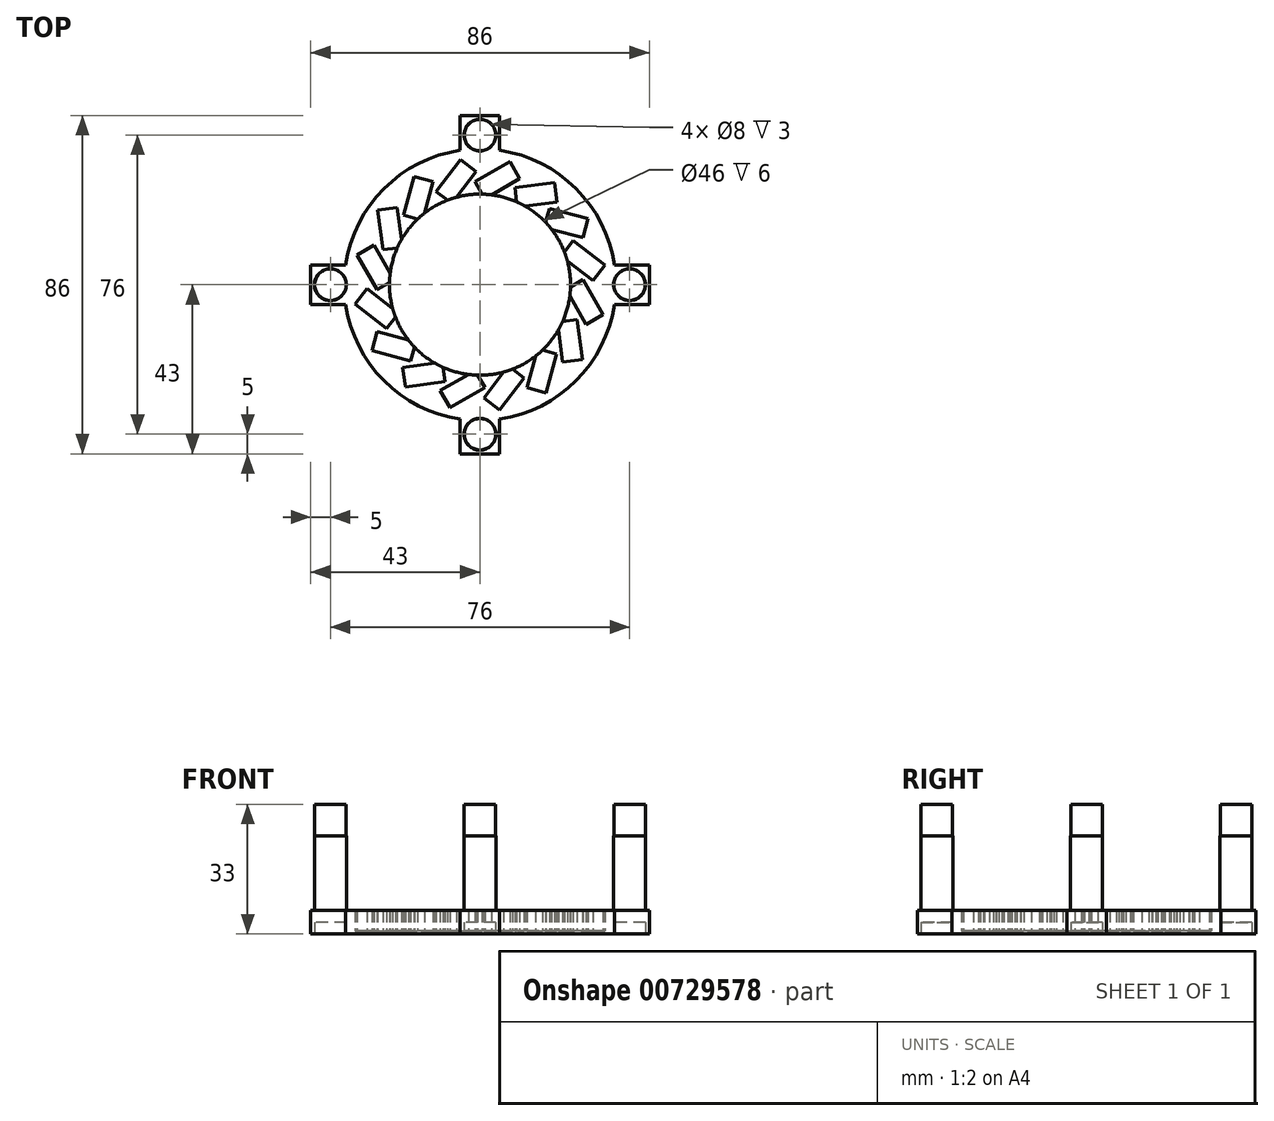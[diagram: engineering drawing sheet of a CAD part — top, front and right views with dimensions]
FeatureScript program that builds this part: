
annotation { "Feature Type Name" : "Feature", "Feature Type Description" : "" }
export const myFeature = defineFeature(function(context is Context, id is Id, definition is map)
    precondition{}
    {
        {
            var Q0;
            Q0=qCreatedBy(makeId("Top.planeOp"),FACE);
            var sketch = newSketch(context, id + "F0", { "sketchPlane" : qUnion([Q0])});
            skCircle(sketch, "E0", {"center": v(0, 0) * mm, "radius": 23 * mm});
            skCircle(sketch, "E1", {"center": v(0, 0) * mm, "radius": 34 * mm});
            skLineSegment(sketch, "E2", {"start": v(0, 0) * mm, "end": v(0, 30) * mm, "construction": true});
            skLineSegment(sketch, "E3.bottom", {"start": v(8.43, 31.47) * mm, "end": v(10.03, 29.56) * mm});
            skLineSegment(sketch, "E3.top", {"start": v(0, 24.4) * mm, "end": v(1.6, 22.48) * mm});
            skLineSegment(sketch, "E3.right", {"start": v(10.03, 29.56) * mm, "end": v(1.6, 22.48) * mm});
            skLineSegment(sketch, "E4.MirrorCS", {"start": v(6.82, 33.39) * mm, "end": v(-1.6, 26.32) * mm});
            skLineSegment(sketch, "E5.MirrorCS", {"start": v(0, 24.4) * mm, "end": v(-1.6, 26.32) * mm});
            skLineSegment(sketch, "E6.MirrorCS", {"start": v(8.43, 31.47) * mm, "end": v(6.82, 33.39) * mm});
            skLineSegment(sketch, "E7", {"start": v(0, 0) * mm, "end": v(35, 0) * mm, "construction": true});
            skSolve(sketch);
        }
        {
            var Q0;
            Q0=qCreatedBy(makeId("Top.planeOp"),FACE);
            var sketch = newSketch(context, id + "F1", { "sketchPlane" : qUnion([Q0])});
            skCircle(sketch, "E8", {"center": v(0, 0) * mm, "radius": 23 * mm});
            skArc(sketch, "E9", {"start": v(-34.4, -2.7) * mm, "mid": v(-24.4, -24.4) * mm, "end": v(-2.7, -34.4) * mm});
            skArc(sketch, "E10", {"start": v(-33.94, -1.95) * mm, "mid": v(-24.04, -24.04) * mm, "end": v(-1.95, -33.94) * mm});
            skLineSegment(sketch, "E11", {"start": v(0, 0) * mm, "end": v(0, 12.6) * mm, "construction": true});
            skLineSegment(sketch, "E12.bottom", {"start": v(8.83, 29.1) * mm, "end": v(10.08, 26.93) * mm});
            skLineSegment(sketch, "E12.top", {"start": v(0, 24) * mm, "end": v(1.25, 21.83) * mm});
            skLineSegment(sketch, "E12.right", {"start": v(10.08, 26.93) * mm, "end": v(1.25, 21.83) * mm});
            skLineSegment(sketch, "E13.MirrorCS", {"start": v(7.58, 31.27) * mm, "end": v(-1.25, 26.17) * mm});
            skLineSegment(sketch, "E14.MirrorCS", {"start": v(0, 24) * mm, "end": v(-1.25, 26.17) * mm});
            skLineSegment(sketch, "E15.MirrorCS", {"start": v(8.83, 29.1) * mm, "end": v(7.58, 31.27) * mm});
            skLineSegment(sketch, "E16", {"start": v(0, 0) * mm, "end": v(34, 0) * mm, "construction": true});
            skLineSegment(sketch, "E17.1.0", {"start": v(-4.96, 31.79) * mm, "end": v(-11.17, 23.7) * mm});
            skLineSegment(sketch, "E17.1.1", {"start": v(-2.98, 30.27) * mm, "end": v(-4.96, 31.79) * mm});
            skLineSegment(sketch, "E17.1.2", {"start": v(-2.98, 30.27) * mm, "end": v(-1, 28.74) * mm});
            skLineSegment(sketch, "E17.1.3", {"start": v(-1, 28.74) * mm, "end": v(-7.2, 20.65) * mm});
            skLineSegment(sketch, "E17.1.4", {"start": v(-9.18, 22.17) * mm, "end": v(-7.2, 20.65) * mm});
            skLineSegment(sketch, "E17.1.5", {"start": v(-9.18, 22.17) * mm, "end": v(-11.17, 23.7) * mm});
            skLineSegment(sketch, "E17.2.0", {"start": v(-16.75, 27.47) * mm, "end": v(-19.39, 17.62) * mm});
            skLineSegment(sketch, "E17.2.1", {"start": v(-14.33, 26.82) * mm, "end": v(-16.75, 27.47) * mm});
            skLineSegment(sketch, "E17.2.2", {"start": v(-14.33, 26.82) * mm, "end": v(-11.92, 26.18) * mm});
            skLineSegment(sketch, "E17.2.3", {"start": v(-11.92, 26.18) * mm, "end": v(-14.56, 16.32) * mm});
            skLineSegment(sketch, "E17.2.4", {"start": v(-16.97, 16.97) * mm, "end": v(-14.56, 16.32) * mm});
            skLineSegment(sketch, "E17.2.5", {"start": v(-16.97, 16.97) * mm, "end": v(-19.39, 17.62) * mm});
            skLineSegment(sketch, "E17.3.0", {"start": v(-25.98, 18.97) * mm, "end": v(-24.65, 8.86) * mm});
            skLineSegment(sketch, "E17.3.1", {"start": v(-23.5, 19.3) * mm, "end": v(-25.98, 18.97) * mm});
            skLineSegment(sketch, "E17.3.2", {"start": v(-23.5, 19.3) * mm, "end": v(-21.03, 19.62) * mm});
            skLineSegment(sketch, "E17.3.3", {"start": v(-21.03, 19.62) * mm, "end": v(-19.7, 9.51) * mm});
            skLineSegment(sketch, "E17.3.4", {"start": v(-22.17, 9.18) * mm, "end": v(-19.7, 9.51) * mm});
            skLineSegment(sketch, "E17.3.5", {"start": v(-22.17, 9.18) * mm, "end": v(-24.65, 8.86) * mm});
            skLineSegment(sketch, "E17.4.0", {"start": v(-31.27, 7.58) * mm, "end": v(-26.17, -1.25) * mm});
            skLineSegment(sketch, "E17.4.1", {"start": v(-29.1, 8.83) * mm, "end": v(-31.27, 7.58) * mm});
            skLineSegment(sketch, "E17.4.2", {"start": v(-29.1, 8.83) * mm, "end": v(-26.93, 10.08) * mm});
            skLineSegment(sketch, "E17.4.3", {"start": v(-26.93, 10.08) * mm, "end": v(-21.83, 1.25) * mm});
            skLineSegment(sketch, "E17.4.4", {"start": v(-24, 0) * mm, "end": v(-21.83, 1.25) * mm});
            skLineSegment(sketch, "E17.4.5", {"start": v(-24, 0) * mm, "end": v(-26.17, -1.25) * mm});
            skLineSegment(sketch, "E17.5.0", {"start": v(-31.79, -4.96) * mm, "end": v(-23.7, -11.17) * mm});
            skLineSegment(sketch, "E17.5.1", {"start": v(-30.27, -2.98) * mm, "end": v(-31.79, -4.96) * mm});
            skLineSegment(sketch, "E17.5.2", {"start": v(-30.27, -2.98) * mm, "end": v(-28.74, -1) * mm});
            skLineSegment(sketch, "E17.5.3", {"start": v(-28.74, -1) * mm, "end": v(-20.65, -7.2) * mm});
            skLineSegment(sketch, "E17.5.4", {"start": v(-22.17, -9.18) * mm, "end": v(-20.65, -7.2) * mm});
            skLineSegment(sketch, "E17.5.5", {"start": v(-22.17, -9.18) * mm, "end": v(-23.7, -11.17) * mm});
            skLineSegment(sketch, "E17.6.0", {"start": v(-27.47, -16.75) * mm, "end": v(-17.62, -19.39) * mm});
            skLineSegment(sketch, "E17.6.1", {"start": v(-26.82, -14.33) * mm, "end": v(-27.47, -16.75) * mm});
            skLineSegment(sketch, "E17.6.2", {"start": v(-26.82, -14.33) * mm, "end": v(-26.18, -11.92) * mm});
            skLineSegment(sketch, "E17.6.3", {"start": v(-26.18, -11.92) * mm, "end": v(-16.32, -14.56) * mm});
            skLineSegment(sketch, "E17.6.4", {"start": v(-16.97, -16.97) * mm, "end": v(-16.32, -14.56) * mm});
            skLineSegment(sketch, "E17.6.5", {"start": v(-16.97, -16.97) * mm, "end": v(-17.62, -19.39) * mm});
            skLineSegment(sketch, "E17.7.0", {"start": v(-18.97, -25.98) * mm, "end": v(-8.86, -24.65) * mm});
            skLineSegment(sketch, "E17.7.1", {"start": v(-19.3, -23.5) * mm, "end": v(-18.97, -25.98) * mm});
            skLineSegment(sketch, "E17.7.2", {"start": v(-19.3, -23.5) * mm, "end": v(-19.62, -21.03) * mm});
            skLineSegment(sketch, "E17.7.3", {"start": v(-19.62, -21.03) * mm, "end": v(-9.51, -19.7) * mm});
            skLineSegment(sketch, "E17.7.4", {"start": v(-9.18, -22.17) * mm, "end": v(-9.51, -19.7) * mm});
            skLineSegment(sketch, "E17.7.5", {"start": v(-9.18, -22.17) * mm, "end": v(-8.86, -24.65) * mm});
            skLineSegment(sketch, "E17.8.0", {"start": v(-7.58, -31.27) * mm, "end": v(1.25, -26.17) * mm});
            skLineSegment(sketch, "E17.8.1", {"start": v(-8.83, -29.1) * mm, "end": v(-7.58, -31.27) * mm});
            skLineSegment(sketch, "E17.8.2", {"start": v(-8.83, -29.1) * mm, "end": v(-10.08, -26.93) * mm});
            skLineSegment(sketch, "E17.8.3", {"start": v(-10.08, -26.93) * mm, "end": v(-1.25, -21.83) * mm});
            skLineSegment(sketch, "E17.8.4", {"start": v(0, -24) * mm, "end": v(-1.25, -21.83) * mm});
            skLineSegment(sketch, "E17.8.5", {"start": v(0, -24) * mm, "end": v(1.25, -26.17) * mm});
            skLineSegment(sketch, "E17.9.0", {"start": v(4.96, -31.79) * mm, "end": v(11.17, -23.7) * mm});
            skLineSegment(sketch, "E17.9.1", {"start": v(2.98, -30.27) * mm, "end": v(4.96, -31.79) * mm});
            skLineSegment(sketch, "E17.9.2", {"start": v(2.98, -30.27) * mm, "end": v(1, -28.74) * mm});
            skLineSegment(sketch, "E17.9.3", {"start": v(1, -28.74) * mm, "end": v(7.2, -20.65) * mm});
            skLineSegment(sketch, "E17.9.4", {"start": v(9.18, -22.17) * mm, "end": v(7.2, -20.65) * mm});
            skLineSegment(sketch, "E17.9.5", {"start": v(9.18, -22.17) * mm, "end": v(11.17, -23.7) * mm});
            skLineSegment(sketch, "E17.10.0", {"start": v(16.75, -27.47) * mm, "end": v(19.39, -17.62) * mm});
            skLineSegment(sketch, "E17.10.1", {"start": v(14.33, -26.82) * mm, "end": v(16.75, -27.47) * mm});
            skLineSegment(sketch, "E17.10.2", {"start": v(14.33, -26.82) * mm, "end": v(11.92, -26.18) * mm});
            skLineSegment(sketch, "E17.10.3", {"start": v(11.92, -26.18) * mm, "end": v(14.56, -16.32) * mm});
            skLineSegment(sketch, "E17.10.4", {"start": v(16.97, -16.97) * mm, "end": v(14.56, -16.32) * mm});
            skLineSegment(sketch, "E17.10.5", {"start": v(16.97, -16.97) * mm, "end": v(19.39, -17.62) * mm});
            skLineSegment(sketch, "E17.11.0", {"start": v(25.98, -18.97) * mm, "end": v(24.65, -8.86) * mm});
            skLineSegment(sketch, "E17.11.1", {"start": v(23.5, -19.3) * mm, "end": v(25.98, -18.97) * mm});
            skLineSegment(sketch, "E17.11.2", {"start": v(23.5, -19.3) * mm, "end": v(21.03, -19.62) * mm});
            skLineSegment(sketch, "E17.11.3", {"start": v(21.03, -19.62) * mm, "end": v(19.7, -9.51) * mm});
            skLineSegment(sketch, "E17.11.4", {"start": v(22.17, -9.18) * mm, "end": v(19.7, -9.51) * mm});
            skLineSegment(sketch, "E17.11.5", {"start": v(22.17, -9.18) * mm, "end": v(24.65, -8.86) * mm});
            skLineSegment(sketch, "E17.12.0", {"start": v(31.27, -7.58) * mm, "end": v(26.17, 1.25) * mm});
            skLineSegment(sketch, "E17.12.1", {"start": v(29.1, -8.83) * mm, "end": v(31.27, -7.58) * mm});
            skLineSegment(sketch, "E17.12.2", {"start": v(29.1, -8.83) * mm, "end": v(26.93, -10.08) * mm});
            skLineSegment(sketch, "E17.12.3", {"start": v(26.93, -10.08) * mm, "end": v(21.83, -1.25) * mm});
            skLineSegment(sketch, "E17.12.4", {"start": v(24, 0) * mm, "end": v(21.83, -1.25) * mm});
            skLineSegment(sketch, "E17.12.5", {"start": v(24, 0) * mm, "end": v(26.17, 1.25) * mm});
            skLineSegment(sketch, "E17.13.0", {"start": v(31.79, 4.96) * mm, "end": v(23.7, 11.17) * mm});
            skLineSegment(sketch, "E17.13.1", {"start": v(30.27, 2.98) * mm, "end": v(31.79, 4.96) * mm});
            skLineSegment(sketch, "E17.13.2", {"start": v(30.27, 2.98) * mm, "end": v(28.74, 1) * mm});
            skLineSegment(sketch, "E17.13.3", {"start": v(28.74, 1) * mm, "end": v(20.65, 7.2) * mm});
            skLineSegment(sketch, "E17.13.4", {"start": v(22.17, 9.18) * mm, "end": v(20.65, 7.2) * mm});
            skLineSegment(sketch, "E17.13.5", {"start": v(22.17, 9.18) * mm, "end": v(23.7, 11.17) * mm});
            skLineSegment(sketch, "E17.14.0", {"start": v(27.47, 16.75) * mm, "end": v(17.62, 19.39) * mm});
            skLineSegment(sketch, "E17.14.1", {"start": v(26.82, 14.33) * mm, "end": v(27.47, 16.75) * mm});
            skLineSegment(sketch, "E17.14.2", {"start": v(26.82, 14.33) * mm, "end": v(26.18, 11.92) * mm});
            skLineSegment(sketch, "E17.14.3", {"start": v(26.18, 11.92) * mm, "end": v(16.32, 14.56) * mm});
            skLineSegment(sketch, "E17.14.4", {"start": v(16.97, 16.97) * mm, "end": v(16.32, 14.56) * mm});
            skLineSegment(sketch, "E17.14.5", {"start": v(16.97, 16.97) * mm, "end": v(17.62, 19.39) * mm});
            skLineSegment(sketch, "E17.15.0", {"start": v(18.97, 25.98) * mm, "end": v(8.86, 24.65) * mm});
            skLineSegment(sketch, "E17.15.1", {"start": v(19.3, 23.5) * mm, "end": v(18.97, 25.98) * mm});
            skLineSegment(sketch, "E17.15.2", {"start": v(19.3, 23.5) * mm, "end": v(19.62, 21.03) * mm});
            skLineSegment(sketch, "E17.15.3", {"start": v(19.62, 21.03) * mm, "end": v(9.51, 19.7) * mm});
            skLineSegment(sketch, "E17.15.4", {"start": v(9.18, 22.17) * mm, "end": v(9.51, 19.7) * mm});
            skLineSegment(sketch, "E17.15.5", {"start": v(9.18, 22.17) * mm, "end": v(8.86, 24.65) * mm});
            skCircle(sketch, "E18", {"center": v(0, 38) * mm, "radius": 4 * mm});
            skCircle(sketch, "E19", {"center": v(0, 38) * mm, "radius": 4.5 * mm});
            skLineSegment(sketch, "E20", {"start": v(0, 42.5) * mm, "end": v(0, 43) * mm});
            skLineSegment(sketch, "E21", {"start": v(0, 43) * mm, "end": v(5, 43) * mm});
            skLineSegment(sketch, "E22", {"start": v(5, 43) * mm, "end": v(5, 34.14) * mm});
            skLineSegment(sketch, "E23.MirrorCS", {"start": v(0, 43) * mm, "end": v(-5, 43) * mm});
            skLineSegment(sketch, "E24.MirrorCS", {"start": v(-5, 43) * mm, "end": v(-5, 34.14) * mm});
            skLineSegment(sketch, "E25.1.0", {"start": v(-43, 0) * mm, "end": v(-43, 5) * mm});
            skLineSegment(sketch, "E25.1.1", {"start": v(-43, 5) * mm, "end": v(-34.14, 5) * mm});
            skLineSegment(sketch, "E25.1.2", {"start": v(-43, 0) * mm, "end": v(-43, -5) * mm});
            skLineSegment(sketch, "E25.1.3", {"start": v(-43, -5) * mm, "end": v(-34.14, -5) * mm});
            skCircle(sketch, "E25.1.4", {"center": v(-38, 0) * mm, "radius": 4.5 * mm});
            skCircle(sketch, "E25.1.5", {"center": v(-38, 0) * mm, "radius": 4 * mm});
            skLineSegment(sketch, "E25.2.0", {"start": v(0, -43) * mm, "end": v(-5, -43) * mm});
            skLineSegment(sketch, "E25.2.1", {"start": v(-5, -43) * mm, "end": v(-5, -34.14) * mm});
            skLineSegment(sketch, "E25.2.2", {"start": v(0, -43) * mm, "end": v(5, -43) * mm});
            skLineSegment(sketch, "E25.2.3", {"start": v(5, -43) * mm, "end": v(5, -34.14) * mm});
            skCircle(sketch, "E25.2.4", {"center": v(0, -38) * mm, "radius": 4.5 * mm});
            skCircle(sketch, "E25.2.5", {"center": v(0, -38) * mm, "radius": 4 * mm});
            skLineSegment(sketch, "E25.3.0", {"start": v(43, 0) * mm, "end": v(43, -5) * mm});
            skLineSegment(sketch, "E25.3.1", {"start": v(43, -5) * mm, "end": v(34.14, -5) * mm});
            skLineSegment(sketch, "E25.3.2", {"start": v(43, 0) * mm, "end": v(43, 5) * mm});
            skLineSegment(sketch, "E25.3.3", {"start": v(43, 5) * mm, "end": v(34.14, 5) * mm});
            skCircle(sketch, "E25.3.4", {"center": v(38, 0) * mm, "radius": 4.5 * mm});
            skCircle(sketch, "E25.3.5", {"center": v(38, 0) * mm, "radius": 4 * mm});
            skArc(sketch, "E26.trimOffspring", {"start": v(33.94, 1.95) * mm, "mid": v(24.04, 24.04) * mm, "end": v(1.95, 33.94) * mm});
            skArc(sketch, "E27.trimOffspring", {"start": v(34.4, 2.7) * mm, "mid": v(24.4, 24.4) * mm, "end": v(2.7, 34.4) * mm});
            skArc(sketch, "E28.trimOffspring", {"start": v(-2.7, 34.4) * mm, "mid": v(-24.4, 24.4) * mm, "end": v(-34.4, 2.7) * mm});
            skArc(sketch, "E29.trimOffspring", {"start": v(2.7, -34.4) * mm, "mid": v(24.4, -24.4) * mm, "end": v(34.4, -2.7) * mm});
            skArc(sketch, "E30.trimOffspring", {"start": v(1.95, -33.94) * mm, "mid": v(24.04, -24.04) * mm, "end": v(33.94, -1.95) * mm});
            skLineSegment(sketch, "E31.trimOffspring", {"start": v(-33.5, 0) * mm, "end": v(-34, 0) * mm});
            skArc(sketch, "E32.trimOffspring", {"start": v(-1.95, 33.94) * mm, "mid": v(-24.04, 24.04) * mm, "end": v(-33.94, 1.95) * mm});
            skCircle(sketch, "E33", {"center": v(0, 38) * mm, "radius": 4.05 * mm});
            skCircle(sketch, "E34.1.0", {"center": v(-38, 0) * mm, "radius": 4.05 * mm});
            skCircle(sketch, "E34.2.0", {"center": v(0, -38) * mm, "radius": 4.05 * mm});
            skCircle(sketch, "E34.3.0", {"center": v(38, 0) * mm, "radius": 4.05 * mm});
            skSolve(sketch);
        }
        {
            var Q0;
            Q0 = qSketchRegion(id + "F1", true);
            var Q1;
            Q1=makeQuery(id+"F1.imprint","IMPRINT",FACE,{"disambiguationData":[TD([[makeQuery(id+"F1.imprint","IMPRINT",EDGE,{"derivedFrom":sQuery(id+"F1.wireOp",EDGE,"d15ed5a5-fd29-49d6-a964-e686c6378fca.3.5")}),1.0]])]});
            var Q2;
            Q2=makeQuery(id+"F1.imprint","IMPRINT",FACE,{"disambiguationData":[TD([[makeQuery(id+"F1.imprint","IMPRINT",EDGE,{"derivedFrom":sQuery(id+"F1.wireOp",EDGE,"d15ed5a5-fd29-49d6-a964-e686c6378fca.3.4")}),1.0]])]});
            var Q3;
            Q3=makeQuery(id+"F1.imprint","IMPRINT",FACE,{"disambiguationData":[TD([[makeQuery(id+"F1.imprint","IMPRINT",EDGE,{"derivedFrom":sQuery(id+"F1.wireOp",EDGE,"nMKEX2UH-BGaZ-hXa7-XY8u-qAvmxy0yM5Br")}),1.0]])]});
            var Q4;
            Q4=makeQuery(id+"F1.imprint","IMPRINT",FACE,{"disambiguationData":[TD([[makeQuery(id+"F1.imprint","IMPRINT",EDGE,{"derivedFrom":sQuery(id+"F1.wireOp",EDGE,"nMKEX2UH-BGaZ-hXa7-XY8u-qAvmxy0yM5Br")}),-1.0]])]});
            var Q5;
            Q5=makeQuery(id+"F1.imprint","IMPRINT",FACE,{"disambiguationData":[TD([[makeQuery(id+"F1.imprint","IMPRINT",EDGE,{"derivedFrom":sQuery(id+"F1.wireOp",EDGE,"d15ed5a5-fd29-49d6-a964-e686c6378fca.1.5")}),1.0]])]});
            var Q6;
            Q6=makeQuery(id+"F1.imprint","IMPRINT",FACE,{"disambiguationData":[TD([[makeQuery(id+"F1.imprint","IMPRINT",EDGE,{"derivedFrom":sQuery(id+"F1.wireOp",EDGE,"d15ed5a5-fd29-49d6-a964-e686c6378fca.1.4")}),1.0]])]});
            var Q7;
            Q7=makeQuery(id+"F1.imprint","IMPRINT",FACE,{"disambiguationData":[TD([[makeQuery(id+"F1.imprint","IMPRINT",EDGE,{"derivedFrom":sQuery(id+"F1.wireOp",EDGE,"d15ed5a5-fd29-49d6-a964-e686c6378fca.2.5")}),1.0]])]});
            var Q8;
            Q8=makeQuery(id+"F1.imprint","IMPRINT",FACE,{"disambiguationData":[TD([[makeQuery(id+"F1.imprint","IMPRINT",EDGE,{"derivedFrom":sQuery(id+"F1.wireOp",EDGE,"d15ed5a5-fd29-49d6-a964-e686c6378fca.2.4")}),1.0]])]});
            var Q9;
            {var subQ98=sQuery(id+"F1.wireOp",EDGE,"E12.bottom");Q9=makeQuery(id+"F1.imprint","IMPRINT",FACE,{"disambiguationData":[TD([[makeQuery(id+"F1.imprint","IMPRINT",EDGE,{"derivedFrom":subQ98}),1.0]])]});}
            var Q10;
            Q10=makeQuery(id+"F1.imprint","IMPRINT",FACE,{"disambiguationData":[TD([[makeQuery(id+"F1.imprint","IMPRINT",EDGE,{"derivedFrom":sQuery(id+"F1.wireOp",EDGE,"E33")}),-1.0]])]});
            var Q11;
            Q11=makeQuery(id+"F1.imprint","IMPRINT",FACE,{"disambiguationData":[TD([[makeQuery(id+"F1.imprint","IMPRINT",EDGE,{"derivedFrom":sQuery(id+"F1.wireOp",EDGE,"E25.2.5")}),-1.0]])]});
            var Q12;
            Q12=makeQuery(id+"F1.imprint","IMPRINT",FACE,{"disambiguationData":[TD([[makeQuery(id+"F1.imprint","IMPRINT",EDGE,{"derivedFrom":sQuery(id+"F1.wireOp",EDGE,"E25.3.5")}),-1.0]])]});
            var Q13;
            Q13=makeQuery(id+"F1.imprint","IMPRINT",FACE,{"disambiguationData":[TD([[makeQuery(id+"F1.imprint","IMPRINT",EDGE,{"derivedFrom":sQuery(id+"F1.wireOp",EDGE,"E25.1.5")}),-1.0]])]});
            var Q14;
            Q14=makeQuery(id+"F1.imprint","IMPRINT",FACE,{"disambiguationData":[TD([[makeQuery(id+"F1.imprint","IMPRINT",EDGE,{"derivedFrom":sQuery(id+"F1.wireOp",EDGE,"E18")}),-1.0]])]});
            var Q15;
            Q15=makeQuery(id+"F1.imprint","IMPRINT",FACE,{"disambiguationData":[TD([[makeQuery(id+"F1.imprint","IMPRINT",EDGE,{"derivedFrom":sQuery(id+"F1.wireOp",EDGE,"E25.1.5")}),-1.0]])]});
            var Q16;
            Q16=makeQuery(id+"F1.imprint","IMPRINT",FACE,{"disambiguationData":[TD([[makeQuery(id+"F1.imprint","IMPRINT",EDGE,{"derivedFrom":sQuery(id+"F1.wireOp",EDGE,"E25.3.5")}),-1.0]])]});
            var Q17;
            Q17=makeQuery(id+"F1.imprint","IMPRINT",FACE,{"disambiguationData":[TD([[makeQuery(id+"F1.imprint","IMPRINT",EDGE,{"derivedFrom":sQuery(id+"F1.wireOp",EDGE,"E25.2.5")}),-1.0]])]});
            var Q18;
            Q18=makeQuery(id+"F1.imprint","IMPRINT",FACE,{"disambiguationData":[TD([[makeQuery(id+"F1.imprint","IMPRINT",EDGE,{"derivedFrom":sQuery(id+"F1.wireOp",EDGE,"E34.3.0")}),-1.0]])]});
            var Q19;
            Q19=makeQuery(id+"F1.imprint","IMPRINT",FACE,{"disambiguationData":[TD([[makeQuery(id+"F1.imprint","IMPRINT",EDGE,{"derivedFrom":sQuery(id+"F1.wireOp",EDGE,"E34.1.0")}),-1.0]])]});
            var Q20;
            Q20=makeQuery(id+"F1.imprint","IMPRINT",FACE,{"disambiguationData":[TD([[makeQuery(id+"F1.imprint","IMPRINT",EDGE,{"derivedFrom":sQuery(id+"F1.wireOp",EDGE,"E34.2.0")}),-1.0]])]});
            extrude(context, id + "F2", {"entities" : qUnion([Q0, Q1, Q2, Q3, Q4, Q5, Q6, Q7, Q8, Q9, Q10, Q11, Q12, Q13, Q14, Q15, Q16, Q17, Q18, Q19, Q20]), "depth" : 6 * mm, "offsetDistance" : 25 * mm});
        }
        {
            var Q0;
            Q0=makeQuery(id+"F1.imprint","IMPRINT",FACE,{"disambiguationData":[TD([[makeQuery(id+"F1.imprint","IMPRINT",EDGE,{"derivedFrom":sQuery(id+"F1.wireOp",EDGE,"E18")}),1.0]])]});
            var Q1;
            Q1=makeQuery(id+"F1.imprint","IMPRINT",FACE,{"disambiguationData":[TD([[makeQuery(id+"F1.imprint","IMPRINT",EDGE,{"derivedFrom":sQuery(id+"F1.wireOp",EDGE,"E25.3.5")}),1.0]])]});
            var Q2;
            Q2=makeQuery(id+"F1.imprint","IMPRINT",FACE,{"disambiguationData":[TD([[makeQuery(id+"F1.imprint","IMPRINT",EDGE,{"derivedFrom":sQuery(id+"F1.wireOp",EDGE,"E18")}),-1.0]])]});
            var Q3;
            Q3=makeQuery(id+"F1.imprint","IMPRINT",FACE,{"disambiguationData":[TD([[makeQuery(id+"F1.imprint","IMPRINT",EDGE,{"derivedFrom":sQuery(id+"F1.wireOp",EDGE,"E25.3.5")}),-1.0]])]});
            var Q4;
            Q4=makeQuery(id+"F1.imprint","IMPRINT",FACE,{"disambiguationData":[TD([[makeQuery(id+"F1.imprint","IMPRINT",EDGE,{"derivedFrom":sQuery(id+"F1.wireOp",EDGE,"E25.2.5")}),1.0]])]});
            var Q5;
            Q5=makeQuery(id+"F1.imprint","IMPRINT",FACE,{"disambiguationData":[TD([[makeQuery(id+"F1.imprint","IMPRINT",EDGE,{"derivedFrom":sQuery(id+"F1.wireOp",EDGE,"E25.2.5")}),-1.0]])]});
            var Q6;
            Q6=makeQuery(id+"F1.imprint","IMPRINT",FACE,{"disambiguationData":[TD([[makeQuery(id+"F1.imprint","IMPRINT",EDGE,{"derivedFrom":sQuery(id+"F1.wireOp",EDGE,"E25.1.5")}),1.0]])]});
            var Q7;
            Q7=makeQuery(id+"F1.imprint","IMPRINT",FACE,{"disambiguationData":[TD([[makeQuery(id+"F1.imprint","IMPRINT",EDGE,{"derivedFrom":sQuery(id+"F1.wireOp",EDGE,"E25.1.5")}),-1.0]])]});
            var Q8;
            Q8=makeQuery(id+"F1.imprint","IMPRINT",FACE,{"disambiguationData":[TD([[makeQuery(id+"F1.imprint","IMPRINT",EDGE,{"derivedFrom":sQuery(id+"F1.wireOp",EDGE,"E25.3.5")}),-1.0]])]});
            var Q9;
            Q9=makeQuery(id+"F1.imprint","IMPRINT",FACE,{"disambiguationData":[TD([[makeQuery(id+"F1.imprint","IMPRINT",EDGE,{"derivedFrom":sQuery(id+"F1.wireOp",EDGE,"E25.1.5")}),-1.0]])]});
            var Q10;
            Q10=makeQuery(id+"F1.imprint","IMPRINT",FACE,{"disambiguationData":[TD([[makeQuery(id+"F1.imprint","IMPRINT",EDGE,{"derivedFrom":sQuery(id+"F1.wireOp",EDGE,"E25.2.5")}),-1.0]])]});
            var Q11;
            Q11=makeQuery(id+"F1.imprint","IMPRINT",FACE,{"disambiguationData":[TD([[makeQuery(id+"F1.imprint","IMPRINT",EDGE,{"derivedFrom":sQuery(id+"F1.wireOp",EDGE,"E25.1.5")}),1.0]])]});
            var Q12;
            Q12=makeQuery(id+"F1.imprint","IMPRINT",FACE,{"disambiguationData":[TD([[makeQuery(id+"F1.imprint","IMPRINT",EDGE,{"derivedFrom":sQuery(id+"F1.wireOp",EDGE,"E25.2.5")}),1.0]])]});
            var Q13;
            Q13=makeQuery(id+"F1.imprint","IMPRINT",FACE,{"disambiguationData":[TD([[makeQuery(id+"F1.imprint","IMPRINT",EDGE,{"derivedFrom":sQuery(id+"F1.wireOp",EDGE,"E25.3.5")}),1.0]])]});
            var Q14;
            Q14=makeQuery(id+"F1.imprint","IMPRINT",FACE,{"disambiguationData":[TD([[makeQuery(id+"F1.imprint","IMPRINT",EDGE,{"derivedFrom":sQuery(id+"F1.wireOp",EDGE,"E25.3.5")}),1.0]])]});
            var Q15;
            Q15=makeQuery(id+"F1.imprint","IMPRINT",FACE,{"disambiguationData":[TD([[makeQuery(id+"F1.imprint","IMPRINT",EDGE,{"derivedFrom":sQuery(id+"F1.wireOp",EDGE,"E25.1.5")}),1.0]])]});
            var Q16;
            Q16=makeQuery(id+"F1.imprint","IMPRINT",FACE,{"disambiguationData":[TD([[makeQuery(id+"F1.imprint","IMPRINT",EDGE,{"derivedFrom":sQuery(id+"F1.wireOp",EDGE,"E25.2.5")}),1.0]])]});
            var Q17;
            Q17=makeQuery(id+"F1.imprint","IMPRINT",FACE,{"disambiguationData":[TD([[makeQuery(id+"F1.imprint","IMPRINT",EDGE,{"derivedFrom":sQuery(id+"F1.wireOp",EDGE,"E25.3.5")}),-1.0]])]});
            var Q18;
            Q18=makeQuery(id+"F1.imprint","IMPRINT",FACE,{"disambiguationData":[TD([[makeQuery(id+"F1.imprint","IMPRINT",EDGE,{"derivedFrom":sQuery(id+"F1.wireOp",EDGE,"E25.2.5")}),-1.0]])]});
            var Q19;
            Q19=makeQuery(id+"F1.imprint","IMPRINT",FACE,{"disambiguationData":[TD([[makeQuery(id+"F1.imprint","IMPRINT",EDGE,{"derivedFrom":sQuery(id+"F1.wireOp",EDGE,"E25.1.5")}),-1.0]])]});
            extrude(context, id + "F3", {"entities" : qUnion([Q0, Q1, Q2, Q3, Q4, Q5, Q6, Q7, Q8, Q9, Q10, Q11, Q12, Q13, Q14, Q15, Q16, Q17, Q18, Q19]), "operationType" : NewBodyOperationType.ADD, "depth" : 25 * mm, "offsetDistance" : 25 * mm});
        }
        {
            var Q0;
            Q0=makeQuery(id+"F1.imprint","IMPRINT",FACE,{"disambiguationData":[TD([[makeQuery(id+"F1.imprint","IMPRINT",EDGE,{"derivedFrom":sQuery(id+"F1.wireOp",EDGE,"E25.1.5")}),1.0]])]});
            var Q1;
            Q1=makeQuery(id+"F1.imprint","IMPRINT",FACE,{"disambiguationData":[TD([[makeQuery(id+"F1.imprint","IMPRINT",EDGE,{"derivedFrom":sQuery(id+"F1.wireOp",EDGE,"E25.3.5")}),1.0]])]});
            var Q2;
            Q2=makeQuery(id+"F1.imprint","IMPRINT",FACE,{"disambiguationData":[TD([[makeQuery(id+"F1.imprint","IMPRINT",EDGE,{"derivedFrom":sQuery(id+"F1.wireOp",EDGE,"E25.2.5")}),1.0]])]});
            var Q3;
            Q3=makeQuery(id+"F1.imprint","IMPRINT",FACE,{"disambiguationData":[TD([[makeQuery(id+"F1.imprint","IMPRINT",EDGE,{"derivedFrom":sQuery(id+"F1.wireOp",EDGE,"E18")}),1.0]])]});
            extrude(context, id + "F4", {"entities" : qUnion([Q0, Q1, Q2, Q3]), "operationType" : NewBodyOperationType.ADD, "depth" : 33 * mm, "offsetDistance" : 25 * mm});
        }
        {
            var Q0;
            Q0=makeQuery(id+"F1.imprint","IMPRINT",FACE,{"disambiguationData":[TD([[makeQuery(id+"F1.imprint","IMPRINT",EDGE,{"derivedFrom":sQuery(id+"F1.wireOp",EDGE,"nMKEX2UH-BGaZ-hXa7-XY8u-qAvmxy0yM5Br")}),1.0]])]});
            var Q1;
            Q1=makeQuery(id+"F1.imprint","IMPRINT",FACE,{"disambiguationData":[TD([[makeQuery(id+"F1.imprint","IMPRINT",EDGE,{"derivedFrom":sQuery(id+"F1.wireOp",EDGE,"d15ed5a5-fd29-49d6-a964-e686c6378fca.1.5")}),1.0]])]});
            var Q2;
            Q2=makeQuery(id+"F1.imprint","IMPRINT",FACE,{"disambiguationData":[TD([[makeQuery(id+"F1.imprint","IMPRINT",EDGE,{"derivedFrom":sQuery(id+"F1.wireOp",EDGE,"d15ed5a5-fd29-49d6-a964-e686c6378fca.3.5")}),1.0]])]});
            var Q3;
            Q3=makeQuery(id+"F1.imprint","IMPRINT",FACE,{"disambiguationData":[TD([[makeQuery(id+"F1.imprint","IMPRINT",EDGE,{"derivedFrom":sQuery(id+"F1.wireOp",EDGE,"d15ed5a5-fd29-49d6-a964-e686c6378fca.2.5")}),1.0]])]});
            var Q4;
            Q4=makeQuery(id+"F1.imprint","IMPRINT",FACE,{"disambiguationData":[TD([[makeQuery(id+"F1.imprint","IMPRINT",EDGE,{"derivedFrom":sQuery(id+"F1.wireOp",EDGE,"E25.1.5")}),1.0]])]});
            var Q5;
            Q5=makeQuery(id+"F1.imprint","IMPRINT",FACE,{"disambiguationData":[TD([[makeQuery(id+"F1.imprint","IMPRINT",EDGE,{"derivedFrom":sQuery(id+"F1.wireOp",EDGE,"E25.3.5")}),1.0]])]});
            var Q6;
            Q6=makeQuery(id+"F1.imprint","IMPRINT",FACE,{"disambiguationData":[TD([[makeQuery(id+"F1.imprint","IMPRINT",EDGE,{"derivedFrom":sQuery(id+"F1.wireOp",EDGE,"E18")}),1.0]])]});
            var Q7;
            Q7=makeQuery(id+"F1.imprint","IMPRINT",FACE,{"disambiguationData":[TD([[makeQuery(id+"F1.imprint","IMPRINT",EDGE,{"derivedFrom":sQuery(id+"F1.wireOp",EDGE,"E25.2.5")}),1.0]])]});
            var Q8;
            Q8=makeQuery(id+"F3.opExtrude","CAP_FACE",FACE,{"disambiguationData":[OSD([sQuery(id+"F1.wireOp",EDGE,"E33")])],"isStart":false});
            var Q9;
            Q9=makeQuery(id+"F1.imprint","IMPRINT",FACE,{"disambiguationData":[TD([[makeQuery(id+"F1.imprint","IMPRINT",EDGE,{"derivedFrom":sQuery(id+"F1.wireOp",EDGE,"E25.3.5")}),1.0]])]});
            var Q10;
            Q10=makeQuery(id+"F1.imprint","IMPRINT",FACE,{"disambiguationData":[TD([[makeQuery(id+"F1.imprint","IMPRINT",EDGE,{"derivedFrom":sQuery(id+"F1.wireOp",EDGE,"E25.2.5")}),1.0]])]});
            var Q11;
            Q11=makeQuery(id+"F1.imprint","IMPRINT",FACE,{"disambiguationData":[TD([[makeQuery(id+"F1.imprint","IMPRINT",EDGE,{"derivedFrom":sQuery(id+"F1.wireOp",EDGE,"E25.1.5")}),1.0]])]});
            extrude(context, id + "F5", {"entities" : qUnion([Q0, Q1, Q2, Q3, Q4, Q5, Q6, Q7, Q8, Q9, Q10, Q11]), "operationType" : NewBodyOperationType.REMOVE, "depth" : 3 * mm, "offsetDistance" : 25 * mm});
        }
        {
            var Q0;
            Q0=makeQuery(id+"F0.imprint","IMPRINT",FACE,{"disambiguationData":[TD([[makeQuery(id+"F0.imprint","IMPRINT",EDGE,{"derivedFrom":sQuery(id+"F0.wireOp",EDGE,"E1")}),1.0]])]});
            var Q1;
            {var subQ1=sQuery(id+"F1.wireOp",EDGE,"E12.bottom");Q1=makeQuery(id+"F1.imprint","IMPRINT",FACE,{"disambiguationData":[TD([[makeQuery(id+"F1.imprint","IMPRINT",EDGE,{"derivedFrom":subQ1}),-1.0]])]});}
            extrude(context, id + "F6", {"entities" : qUnion([Q0, Q1]), "operationType" : NewBodyOperationType.ADD, "depth" : 0.8 * mm, "offsetDistance" : 25 * mm});
        }
    });
